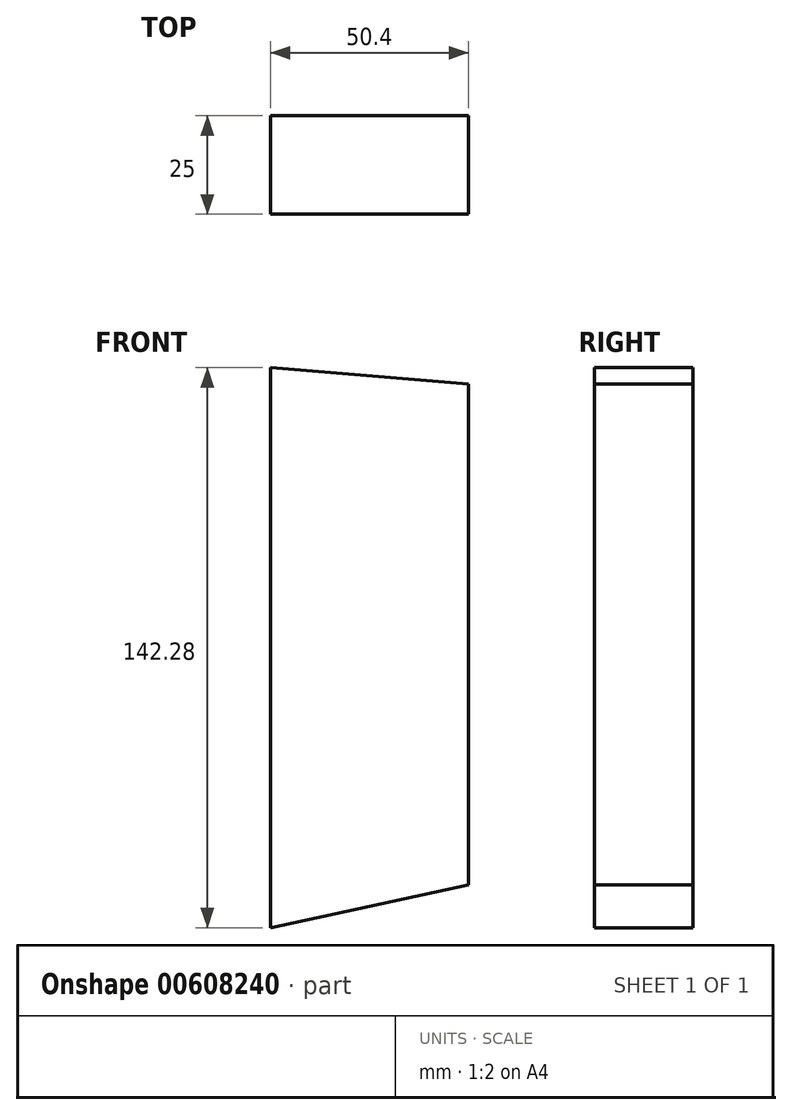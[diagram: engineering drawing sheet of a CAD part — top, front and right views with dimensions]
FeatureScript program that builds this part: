
annotation { "Feature Type Name" : "Feature", "Feature Type Description" : "" }
export const myFeature = defineFeature(function(context is Context, id is Id, definition is map)
    precondition{}
    {
        {
            var Q0;
            Q0=qCreatedBy(makeId("Front.planeOp"),FACE);
            var sketch = newSketch(context, id + "F0", { "sketchPlane" : qUnion([Q0])});
            skLineSegment(sketch, "E0", {"start": v(-50.4, 55.6) * mm, "end": v(-50.4, -86.7) * mm});
            skLineSegment(sketch, "E1", {"start": v(-50.4, -86.7) * mm, "end": v(0, -75.86) * mm});
            skLineSegment(sketch, "E2", {"start": v(0, -75.86) * mm, "end": v(0, 51.42) * mm});
            skLineSegment(sketch, "E3", {"start": v(0, 51.42) * mm, "end": v(-50.4, 55.6) * mm});
            skSolve(sketch);
        }
        {
            var Q0;
            Q0 = qSketchRegion(id + "F0", true);
            extrude(context, id + "F1", {"entities" : qUnion([Q0]), "depth" : 25 * mm, "offsetDistance" : 25 * mm});
        }
    });
